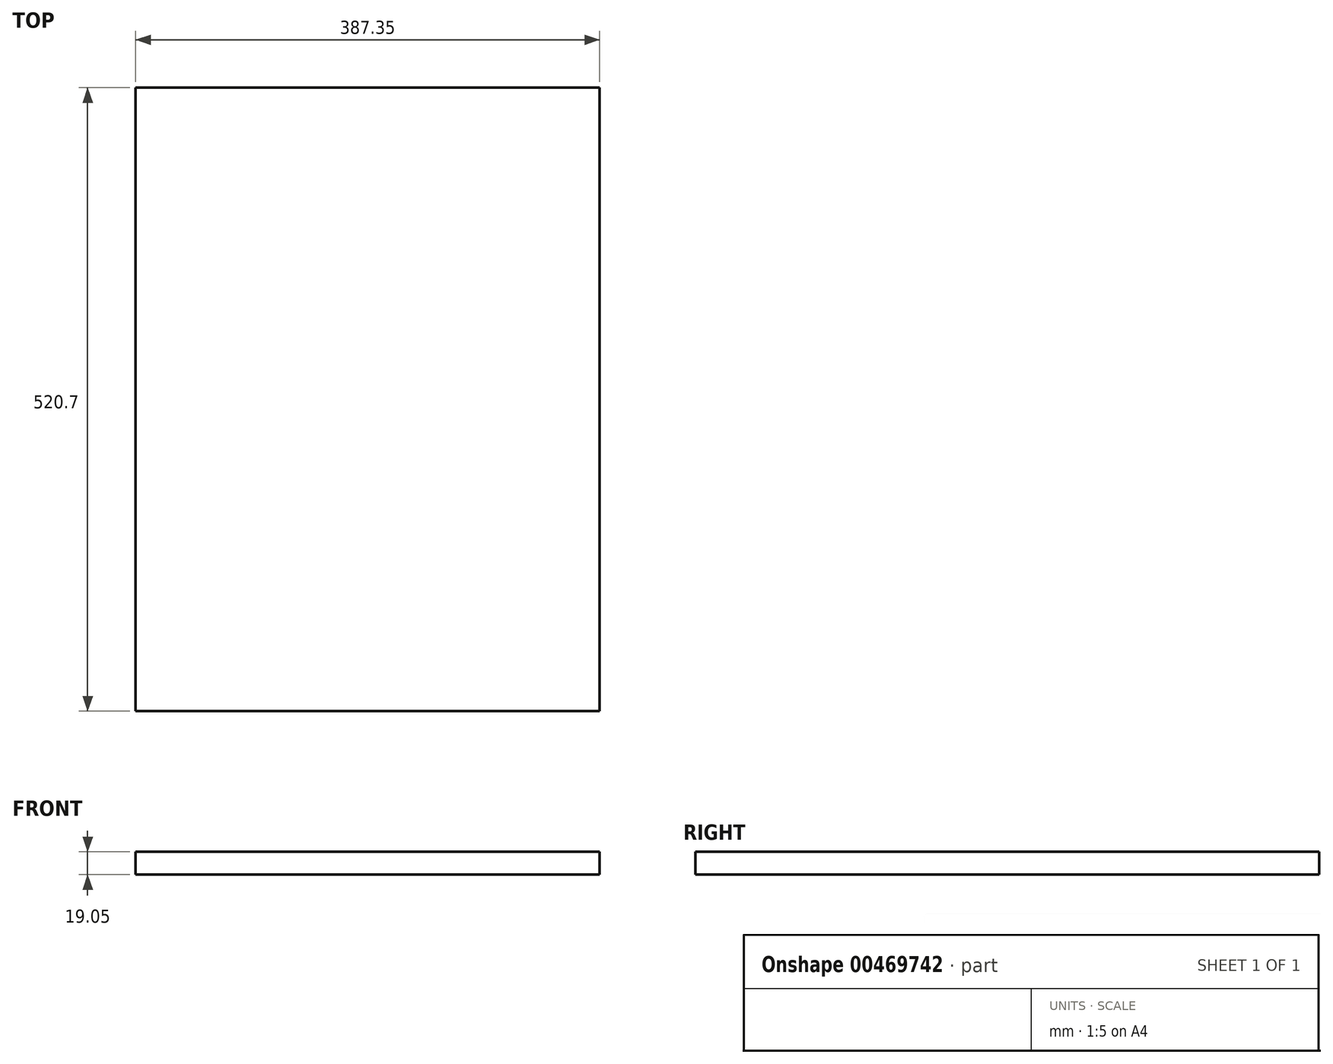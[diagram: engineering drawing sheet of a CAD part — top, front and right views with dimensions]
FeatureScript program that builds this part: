
annotation { "Feature Type Name" : "Feature", "Feature Type Description" : "" }
export const myFeature = defineFeature(function(context is Context, id is Id, definition is map)
    precondition{}
    {
        {
            var Q0;
            Q0=qCreatedBy(makeId("Front.planeOp"),FACE);
            var sketch = newSketch(context, id + "F0", { "sketchPlane" : qUnion([Q0])});
            skLineSegment(sketch, "E0.bottom", {"start": v(0, 0) * mm, "end": v(387.35, 0) * mm});
            skLineSegment(sketch, "E0.top", {"start": v(0, 19.05) * mm, "end": v(387.35, 19.05) * mm});
            skLineSegment(sketch, "E0.left", {"start": v(0, 0) * mm, "end": v(0, 19.05) * mm});
            skLineSegment(sketch, "E0.right", {"start": v(387.35, 0) * mm, "end": v(387.35, 19.05) * mm});
            skSolve(sketch);
        }
        {
            var Q0;
            Q0=makeQuery(id+"F0.imprint","IMPRINT",FACE,{"disambiguationData":[TD([[makeQuery(id+"F0.imprint","IMPRINT",EDGE,{"derivedFrom":sQuery(id+"F0.wireOp",EDGE,"E0.bottom")}),1.0]])]});
            extrude(context, id + "F1", {"entities" : qUnion([Q0]), "depth" : 520.7 * mm, "offsetDistance" : 25.4 * mm});
        }
    });
